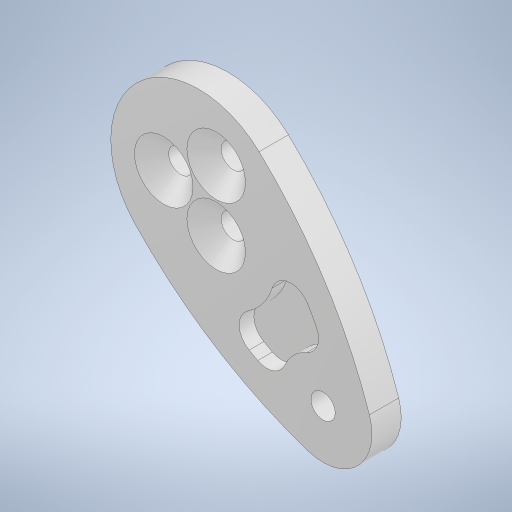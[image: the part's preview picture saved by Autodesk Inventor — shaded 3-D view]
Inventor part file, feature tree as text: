
AUTODESK INVENTOR PART (.ipt)
format: ipt  version: 2023.1 (Build 271208000, 208)  size: 333,312 bytes
history: native  units: mm
features: extrude x2, sketch x2, chamfer x1
ambient origin geometry x8: Origin, YZ Plane, XZ Plane, XY Plane, X Axis, Y Axis, Z Axis, Center Point
bodies: Solid2 (feature_tree)
feature tree (5):
  extrude  "Extrusion2"  Depth=3.0mm TaperAngle=0.0deg
  chamfer  "Chamfer3"  Distance=2.0mm Angle=45.0deg
  extrude  "Extrusion3"  Depth=2.0mm
  sketch  "Sketch2"  dims[d46=30.0mm d47=18.0mm d48=135.0deg d49=5.0mm d50=18.0mm d54=8.0mm d55=10.0mm d56=6.05mm d57=2.5mm d58=18.0mm d59=135.0deg d60=5.0mm d61=18.0mm d62=2.5mm d63=6.2mm d64=360.0deg d65=8.0mm d66=10.0mm d67=6.05mm d68=2.5mm d69=3.0mm d70=0.0mm d74=1.75mm d75=2.0mm d76=45.0deg]
  sketch  "Sketch3"  dims[d77=3.0mm d78=2.0mm d79=2.0mm d80=3.0mm d81=3.0mm d82=2.0mm d83=2.0mm d84=3.0mm d85=1.5mm d86=0.0mm]
